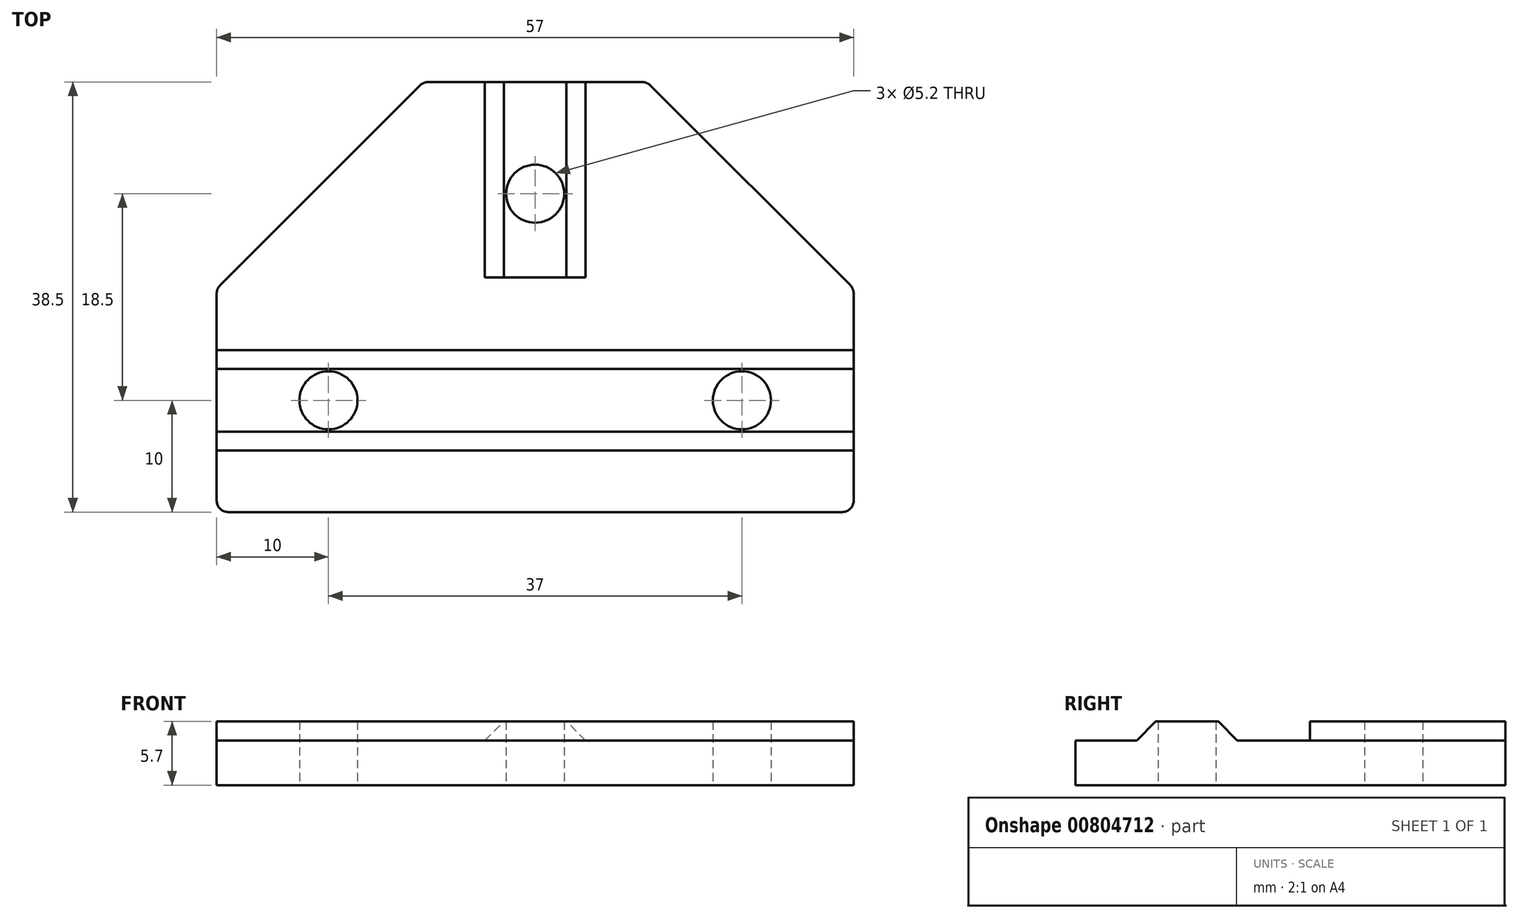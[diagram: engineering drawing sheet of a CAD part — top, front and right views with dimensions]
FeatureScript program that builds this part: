
annotation { "Feature Type Name" : "Feature", "Feature Type Description" : "" }
export const myFeature = defineFeature(function(context is Context, id is Id, definition is map)
    precondition{}
    {
        {
            var Q0;
            Q0=qCreatedBy(makeId("Top.planeOp"),FACE);
            var sketch = newSketch(context, id + "F0", { "sketchPlane" : qUnion([Q0])});
            skLineSegment(sketch, "E0", {"start": v(0, 0) * mm, "end": v(-28.5, 0) * mm});
            skLineSegment(sketch, "E1", {"start": v(-28.5, 0) * mm, "end": v(-28.5, 20) * mm});
            skLineSegment(sketch, "E2", {"start": v(0, 38.5) * mm, "end": v(0, 31.1) * mm});
            skCircle(sketch, "E3", {"center": v(-18.5, 10) * mm, "radius": 2.6 * mm});
            skArc(sketch, "E4", {"start": v(0, 31.1) * mm, "mid": v(-2.6, 28.5) * mm, "end": v(0, 25.9) * mm});
            skLineSegment(sketch, "E5", {"start": v(0, 38.5) * mm, "end": v(-10, 38.5) * mm});
            skLineSegment(sketch, "E6", {"start": v(-10, 38.5) * mm, "end": v(-28.5, 20) * mm});
            skLineSegment(sketch, "E7.trimOffspring", {"start": v(0, 25.9) * mm, "end": v(0, 0) * mm});
            skSolve(sketch);
        }
        {
            var Q0;
            Q0=qSketchRegion(id+"F0",true);
            extrude(context, id + "F1", {"entities" : qUnion([Q0]), "depth" : 4 * mm, "offsetDistance" : 25 * mm});
        }
        {
            var Q0;
            Q0=makeQuery(id+"F1.opExtrude","CAP_FACE",FACE,{"disambiguationData":[OSD([sQuery(id+"F0.wireOp",EDGE,"E0"),sQuery(id+"F0.wireOp",EDGE,"E1"),sQuery(id+"F0.wireOp",EDGE,"E2"),sQuery(id+"F0.wireOp",EDGE,"E3"),sQuery(id+"F0.wireOp",EDGE,"E4"),sQuery(id+"F0.wireOp",EDGE,"E5"),sQuery(id+"F0.wireOp",EDGE,"E6"),sQuery(id+"F0.wireOp",EDGE,"E7.trimOffspring")])],"isStart":false});
            var sketch = newSketch(context, id + "F2", { "sketchPlane" : qUnion([Q0])});
            skLineSegment(sketch, "E8.bottom", {"start": v(-28.5, 14.5) * mm, "end": v(0, 14.5) * mm});
            skLineSegment(sketch, "E8.top", {"start": v(-28.5, 5.5) * mm, "end": v(0, 5.5) * mm});
            skLineSegment(sketch, "E8.left", {"start": v(-28.5, 14.5) * mm, "end": v(-28.5, 5.5) * mm});
            skLineSegment(sketch, "E8.right", {"start": v(0, 14.5) * mm, "end": v(0, 5.5) * mm});
            skCircle(sketch, "E9.0", {"center": v(-18.5, 10) * mm, "radius": 2.6 * mm});
            skArc(sketch, "E10.0", {"start": v(0, 31.1) * mm, "mid": v(-2.6, 28.5) * mm, "end": v(0, 25.9) * mm});
            skLineSegment(sketch, "E11", {"start": v(0, 38.5) * mm, "end": v(-4.5, 38.5) * mm});
            skLineSegment(sketch, "E12", {"start": v(-4.5, 38.5) * mm, "end": v(-4.5, 21) * mm});
            skLineSegment(sketch, "E13", {"start": v(-4.5, 21) * mm, "end": v(0, 21) * mm});
            skLineSegment(sketch, "E14", {"start": v(0, 25.9) * mm, "end": v(0, 21) * mm});
            skLineSegment(sketch, "E15", {"start": v(0, 38.5) * mm, "end": v(0, 31.1) * mm});
            skSolve(sketch);
        }
        {
            var Q0;
            Q0=qSketchRegion(id+"F2",true);
            extrude(context, id + "F3", {"entities" : qUnion([Q0]), "operationType" : NewBodyOperationType.ADD, "depth" : 1.7 * mm, "offsetDistance" : 25 * mm});
        }
        {
            var Q0;
            Q0=makeQuery(id+"F3.opExtrude","CAP_EDGE",EDGE,{"disambiguationData":[OSD([sQuery(id+"F2.wireOp",EDGE,"E8.bottom")])],"isStart":false});
            var Q1;
            Q1=makeQuery(id+"F3.opExtrude","CAP_EDGE",EDGE,{"disambiguationData":[OSD([sQuery(id+"F2.wireOp",EDGE,"E8.top")])],"isStart":false});
            var Q2;
            Q2=makeQuery(id+"F3.opExtrude","CAP_EDGE",EDGE,{"disambiguationData":[OSD([sQuery(id+"F2.wireOp",EDGE,"E12")])],"isStart":false});
            chamfer(context, id + "F4", {"entities" : qUnion([Q0, Q1, Q2]), "width" : 1.7 * mm, "tangentPropagation" : true});
        }
        {
            var Q0;
            Q0=makeQuery(id+"F1.opExtrude","SWEPT_EDGE",EDGE,{"disambiguationData":[OSD([sQuery(id+"F0.wireOp",EDGE,"E5"),sQuery(id+"F0.wireOp",EDGE,"E6")])]});
            var Q1;
            Q1=makeQuery(id+"F1.opExtrude","SWEPT_EDGE",EDGE,{"disambiguationData":[OSD([sQuery(id+"F0.wireOp",EDGE,"E1"),sQuery(id+"F0.wireOp",EDGE,"E6")])]});
            var Q2;
            Q2=makeQuery(id+"F1.opExtrude","SWEPT_EDGE",EDGE,{"disambiguationData":[OSD([sQuery(id+"F0.wireOp",EDGE,"E0"),sQuery(id+"F0.wireOp",EDGE,"E1")])]});
            fillet(context, id + "F5", {"entities" : qUnion([Q0, Q1, Q2]), "radius" : 1 * mm, "tangentPropagation" : true, "allowEdgeOverflow" : false});
        }
        {
            var Q0;
            Q0=makeQuery(id+"F1.opExtrude","SWEPT_BODY",BODY,{"disambiguationData":[OSD([sQuery(id+"F0.wireOp",EDGE,"E0"),sQuery(id+"F0.wireOp",EDGE,"E1"),sQuery(id+"F0.wireOp",EDGE,"E2"),sQuery(id+"F0.wireOp",EDGE,"E3"),sQuery(id+"F0.wireOp",EDGE,"E4"),sQuery(id+"F0.wireOp",EDGE,"E5"),sQuery(id+"F0.wireOp",EDGE,"E6"),sQuery(id+"F0.wireOp",EDGE,"E7.trimOffspring")])]});
            var Q1;
            Q1=makeQuery(id+"F3.boolean.opBoolean","MERGE",FACE,{"derivedFrom":[makeQuery(id+"F1.opExtrude","SWEPT_FACE",FACE,{"disambiguationData":[OSD([sQuery(id+"F0.wireOp",EDGE,"E2")])]}),makeQuery(id+"F3.opExtrude","SWEPT_FACE",FACE,{"disambiguationData":[OSD([sQuery(id+"F2.wireOp",EDGE,"E15")])]})]});
            mirror(context, id + "F6", {"operationType" : NewBodyOperationType.ADD, "entities" : qUnion([Q0]), "mirrorPlane" : qUnion([Q1])});
        }
    });
